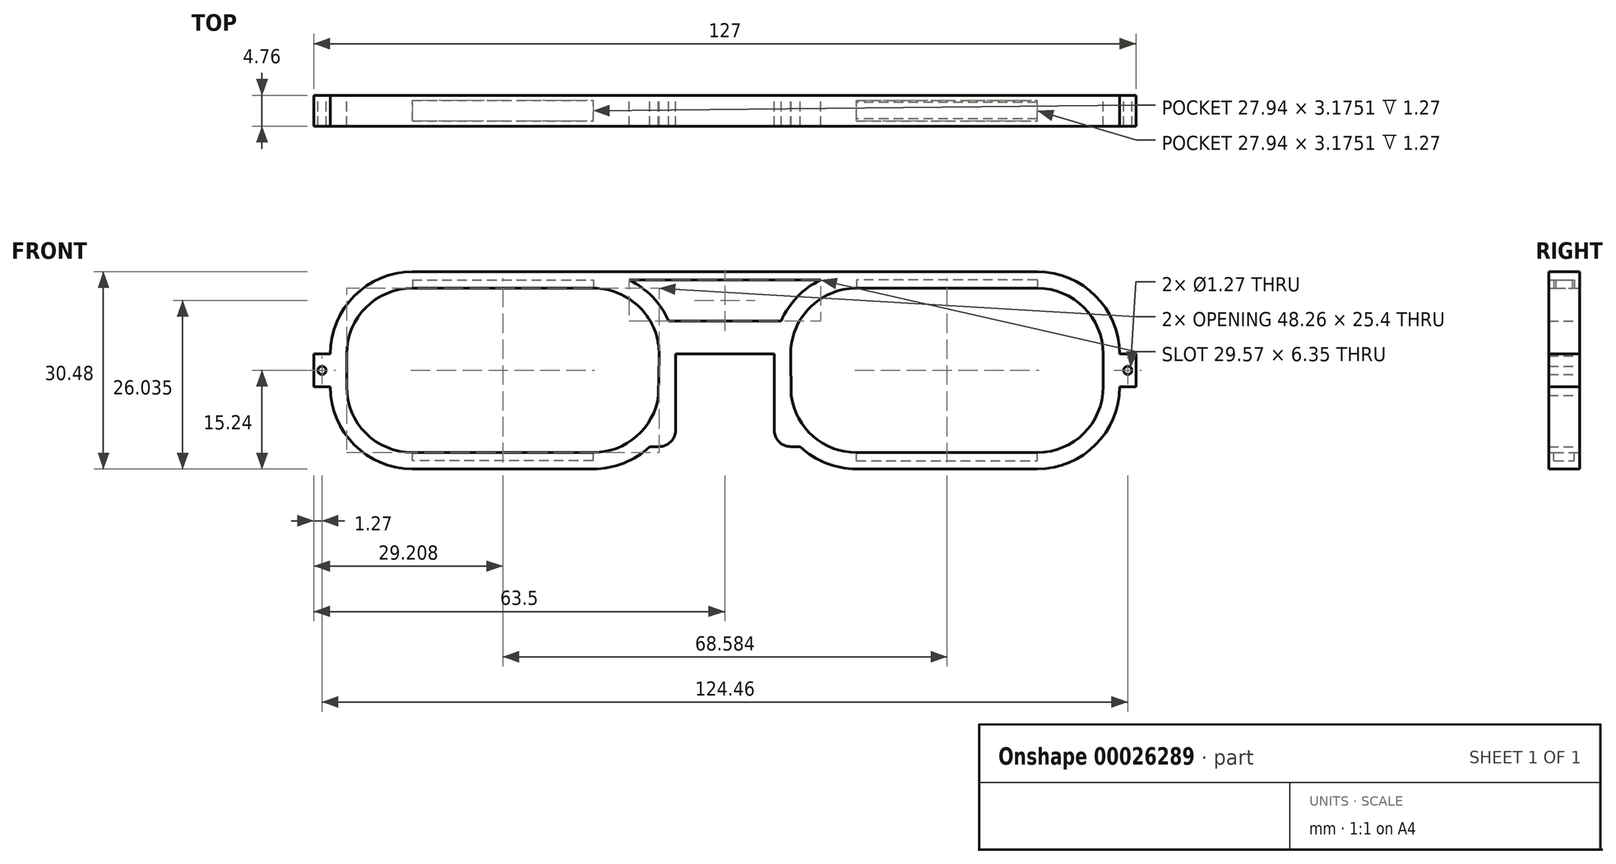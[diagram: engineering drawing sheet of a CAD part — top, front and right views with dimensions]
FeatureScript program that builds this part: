
annotation { "Feature Type Name" : "Feature", "Feature Type Description" : "" }
export const myFeature = defineFeature(function(context is Context, id is Id, definition is map)
    precondition{}
    {
        {
            var Q0;
            Q0=qCreatedBy(makeId("Front.planeOp"),FACE);
            var sketch = newSketch(context, id + "F0", { "sketchPlane" : qUnion([Q0])});
            skLineSegment(sketch, "E0.bottom", {"start": v(12.7, 0) * mm, "end": v(40.64, 0) * mm});
            skLineSegment(sketch, "E0.top", {"start": v(12.7, 30.48) * mm, "end": v(40.64, 30.48) * mm});
            skLineSegment(sketch, "E0.left", {"start": v(0, 12.7) * mm, "end": v(0, 17.78) * mm});
            skLineSegment(sketch, "E0.right", {"start": v(53.34, 12.7) * mm, "end": v(53.34, 17.78) * mm});
            skPoint(sketch, "E1.visualSharp", {"position": v(0, 30.48) * mm});
            skArc(sketch, "E1.filletArc", {"start": v(12.7, 30.48) * mm, "mid": v(3.72, 26.76) * mm, "end": v(0, 17.78) * mm});
            skPoint(sketch, "E2.visualSharp", {"position": v(0, 0) * mm});
            skArc(sketch, "E2.filletArc", {"start": v(0, 12.7) * mm, "mid": v(3.72, 3.72) * mm, "end": v(12.7, 0) * mm});
            skPoint(sketch, "E3.visualSharp", {"position": v(53.34, 0) * mm});
            skArc(sketch, "E3.filletArc", {"start": v(40.64, 0) * mm, "mid": v(45.33, 0.9) * mm, "end": v(49.36, 3.46) * mm});
            skArc(sketch, "E4.filletArc", {"start": v(52.28, 22.86) * mm, "mid": v(49.8, 26.58) * mm, "end": v(46.18, 29.21) * mm});
            skLineSegment(sketch, "E5", {"start": v(40.64, 30.48) * mm, "end": v(68.58, 30.48) * mm});
            skLineSegment(sketch, "E6.MirrorCS", {"start": v(81.28, 30.48) * mm, "end": v(53.34, 30.48) * mm});
            skArc(sketch, "E7.MirrorCS", {"start": v(69.64, 22.86) * mm, "mid": v(72.12, 26.58) * mm, "end": v(75.74, 29.21) * mm});
            skLineSegment(sketch, "E8.MirrorCS", {"start": v(68.58, 12.7) * mm, "end": v(68.58, 17.78) * mm});
            skArc(sketch, "E9.MirrorCS", {"start": v(81.28, 0) * mm, "mid": v(76.6, 0.9) * mm, "end": v(72.56, 3.46) * mm});
            skLineSegment(sketch, "E10.MirrorCS", {"start": v(109.22, 0) * mm, "end": v(81.28, 0) * mm});
            skArc(sketch, "E11.MirrorCS", {"start": v(121.92, 12.7) * mm, "mid": v(118.2, 3.72) * mm, "end": v(109.22, 0) * mm});
            skLineSegment(sketch, "E12.MirrorCS", {"start": v(121.92, 12.7) * mm, "end": v(121.92, 17.78) * mm});
            skArc(sketch, "E13.MirrorCS", {"start": v(109.22, 30.48) * mm, "mid": v(118.2, 26.76) * mm, "end": v(121.92, 17.78) * mm});
            skLineSegment(sketch, "E14.MirrorCS", {"start": v(109.22, 30.48) * mm, "end": v(81.28, 30.48) * mm});
            skLineSegment(sketch, "E15", {"start": v(46.18, 29.21) * mm, "end": v(75.74, 29.21) * mm});
            skLineSegment(sketch, "E16", {"start": v(53.34, 17.78) * mm, "end": v(68.58, 17.78) * mm});
            skLineSegment(sketch, "E17", {"start": v(52.28, 22.86) * mm, "end": v(69.64, 22.86) * mm});
            skPoint(sketch, "E18.end.orphan", {"position": v(53.34, 22.86) * mm});
            skLineSegment(sketch, "E19", {"start": v(53.34, 12.7) * mm, "end": v(53.34, 6) * mm});
            skLineSegment(sketch, "E20", {"start": v(50.8, 3.46) * mm, "end": v(49.36, 3.46) * mm});
            skPoint(sketch, "E21.visualSharp", {"position": v(53.34, 3.46) * mm});
            skArc(sketch, "E21.filletArc", {"start": v(50.8, 3.46) * mm, "mid": v(52.6, 4.2) * mm, "end": v(53.34, 6) * mm});
            skLineSegment(sketch, "E22", {"start": v(68.58, 12.7) * mm, "end": v(68.58, 6) * mm});
            skLineSegment(sketch, "E23", {"start": v(71.12, 3.46) * mm, "end": v(72.56, 3.46) * mm});
            skPoint(sketch, "E24.visualSharp", {"position": v(68.58, 3.46) * mm});
            skArc(sketch, "E24.filletArc", {"start": v(68.58, 6) * mm, "mid": v(69.32, 4.2) * mm, "end": v(71.12, 3.46) * mm});
            skArc(sketch, "E25", {"start": v(81.28, 27.94) * mm, "mid": v(74, 24.86) * mm, "end": v(71.12, 17.5) * mm});
            skArc(sketch, "E26", {"start": v(119.38, 17.78) * mm, "mid": v(116.4, 24.96) * mm, "end": v(109.22, 27.94) * mm});
            skArc(sketch, "E27", {"start": v(71.2, 11.36) * mm, "mid": v(74.59, 5.06) * mm, "end": v(81.28, 2.54) * mm});
            skArc(sketch, "E28", {"start": v(109.22, 2.54) * mm, "mid": v(116.4, 5.52) * mm, "end": v(119.38, 12.7) * mm});
            skLineSegment(sketch, "E29", {"start": v(71.12, 17.78) * mm, "end": v(71.2, 11.36) * mm});
            skLineSegment(sketch, "E30", {"start": v(81.28, 27.94) * mm, "end": v(109.22, 27.94) * mm});
            skLineSegment(sketch, "E31", {"start": v(119.38, 17.78) * mm, "end": v(119.38, 12.7) * mm});
            skLineSegment(sketch, "E32", {"start": v(109.22, 2.54) * mm, "end": v(81.28, 2.54) * mm});
            skArc(sketch, "E33.MirrorCS", {"start": v(40.64, 27.94) * mm, "mid": v(47.92, 24.86) * mm, "end": v(50.8, 17.5) * mm});
            skLineSegment(sketch, "E34.MirrorCS", {"start": v(50.8, 17.78) * mm, "end": v(50.71, 11.36) * mm});
            skArc(sketch, "E35.MirrorCS", {"start": v(50.71, 11.36) * mm, "mid": v(47.33, 5.06) * mm, "end": v(40.64, 2.54) * mm});
            skLineSegment(sketch, "E36.MirrorCS", {"start": v(12.7, 2.54) * mm, "end": v(40.64, 2.54) * mm});
            skArc(sketch, "E37.MirrorCS", {"start": v(12.7, 2.54) * mm, "mid": v(5.52, 5.52) * mm, "end": v(2.54, 12.7) * mm});
            skArc(sketch, "E38.MirrorCS", {"start": v(2.54, 17.78) * mm, "mid": v(5.52, 24.96) * mm, "end": v(12.7, 27.94) * mm});
            skLineSegment(sketch, "E39.MirrorCS", {"start": v(40.64, 27.94) * mm, "end": v(12.7, 27.94) * mm});
            skLineSegment(sketch, "E40.bottom", {"start": v(121.92, 17.78) * mm, "end": v(124.46, 17.78) * mm});
            skLineSegment(sketch, "E40.top", {"start": v(121.92, 12.7) * mm, "end": v(124.46, 12.7) * mm});
            skLineSegment(sketch, "E40.left", {"start": v(121.92, 17.78) * mm, "end": v(121.92, 12.7) * mm});
            skLineSegment(sketch, "E40.right", {"start": v(124.46, 17.78) * mm, "end": v(124.46, 12.7) * mm});
            skLineSegment(sketch, "E41", {"start": v(2.54, 17.78) * mm, "end": v(2.54, 12.7) * mm});
            skLineSegment(sketch, "E42.bottom", {"start": v(0, 17.78) * mm, "end": v(-2.54, 17.78) * mm});
            skLineSegment(sketch, "E42.top", {"start": v(0, 12.7) * mm, "end": v(-2.54, 12.7) * mm});
            skLineSegment(sketch, "E42.left", {"start": v(0, 17.78) * mm, "end": v(0, 12.7) * mm});
            skLineSegment(sketch, "E42.right", {"start": v(-2.54, 17.78) * mm, "end": v(-2.54, 12.7) * mm});
            skLineSegment(sketch, "E43", {"start": v(121.92, 15.24) * mm, "end": v(124.46, 15.24) * mm});
            skLineSegment(sketch, "E44", {"start": v(0, 15.24) * mm, "end": v(-2.54, 15.24) * mm});
            skCircle(sketch, "E45", {"center": v(-1.27, 15.24) * mm, "radius": 0.64 * mm});
            skCircle(sketch, "E46", {"center": v(123.19, 15.24) * mm, "radius": 0.64 * mm});
            skSolve(sketch);
        }
        {
            var Q0;
            Q0=makeQuery(id+"F0.imprint","IMPRINT",FACE,{"disambiguationData":[TD([[makeQuery(id+"F0.imprint","IMPRINT",EDGE,{"derivedFrom":sQuery(id+"F0.wireOp",EDGE,"E0.bottom")}),1.0]])]});
            var Q1;
            {var subQ8=sQuery(id+"F0.wireOp",EDGE,"E42.bottom");Q1=makeQuery(id+"F0.imprint","IMPRINT",FACE,{"disambiguationData":[TD([[makeQuery(id+"F0.imprint","IMPRINT",EDGE,{"derivedFrom":subQ8}),1.0]])]});}
            var Q2;
            {var subQ8=sQuery(id+"F0.wireOp",EDGE,"E42.top");Q2=makeQuery(id+"F0.imprint","IMPRINT",FACE,{"disambiguationData":[TD([[makeQuery(id+"F0.imprint","IMPRINT",EDGE,{"derivedFrom":subQ8}),-1.0]])]});}
            var Q3;
            {var subQ8=sQuery(id+"F0.wireOp",EDGE,"E40.bottom");Q3=makeQuery(id+"F0.imprint","IMPRINT",FACE,{"disambiguationData":[TD([[makeQuery(id+"F0.imprint","IMPRINT",EDGE,{"derivedFrom":subQ8}),-1.0]])]});}
            var Q4;
            {var subQ8=sQuery(id+"F0.wireOp",EDGE,"E40.top");Q4=makeQuery(id+"F0.imprint","IMPRINT",FACE,{"disambiguationData":[TD([[makeQuery(id+"F0.imprint","IMPRINT",EDGE,{"derivedFrom":subQ8}),1.0]])]});}
            extrude(context, id + "F1", {"entities" : qUnion([Q0, Q1, Q2, Q3, Q4]), "depth" : 4.76 * mm});
        }
        {
            var Q0;
            Q0=makeQuery(id+"F1.opExtrude","SWEPT_FACE",FACE,{"disambiguationData":[OSD([sQuery(id+"F0.wireOp",EDGE,"E36.MirrorCS")])]});
            var sketch = newSketch(context, id + "F2", { "sketchPlane" : qUnion([Q0])});
            skLineSegment(sketch, "E47.1", {"start": v(40.64, -4.76) * mm, "end": v(40.64, 0) * mm});
            skLineSegment(sketch, "E47.2", {"start": v(12.7, 0) * mm, "end": v(40.64, 0) * mm});
            skLineSegment(sketch, "E47.3", {"start": v(12.7, -4.76) * mm, "end": v(40.64, -4.76) * mm});
            skLineSegment(sketch, "E47.4", {"start": v(12.7, -4.76) * mm, "end": v(12.7, 0) * mm});
            skLineSegment(sketch, "E48", {"start": v(12.7, -2.38) * mm, "end": v(40.64, -2.38) * mm});
            skLineSegment(sketch, "E49", {"start": v(40.64, -2.38) * mm, "end": v(40.64, -0.8) * mm});
            skLineSegment(sketch, "E50", {"start": v(40.64, -0.8) * mm, "end": v(12.7, -0.8) * mm});
            skLineSegment(sketch, "E51.MirrorCS", {"start": v(40.64, -3.97) * mm, "end": v(12.7, -3.97) * mm});
            skSolve(sketch);
        }
        {
            var Q0;
            {var subQ1=sQuery(id+"F2.wireOp",EDGE,"E48");Q0=makeQuery(id+"F2.imprint","IMPRINT",FACE,{"disambiguationData":[TD([[makeQuery(id+"F2.imprint","IMPRINT",EDGE,{"derivedFrom":subQ1}),1.0]])]});}
            var Q1;
            {var subQ1=sQuery(id+"F2.wireOp",EDGE,"E48");Q1=makeQuery(id+"F2.imprint","IMPRINT",FACE,{"disambiguationData":[TD([[makeQuery(id+"F2.imprint","IMPRINT",EDGE,{"derivedFrom":subQ1}),-1.0]])]});}
            extrude(context, id + "F3", {"entities" : qUnion([Q0, Q1]), "operationType" : NewBodyOperationType.REMOVE, "oppositeDirection" : true, "depth" : 1.27 * mm});
        }
        {
            var Q0;
            Q0=makeQuery(id+"F1.opExtrude","SWEPT_FACE",FACE,{"disambiguationData":[OSD([sQuery(id+"F0.wireOp",EDGE,"E39.MirrorCS")])]});
            var sketch = newSketch(context, id + "F4", { "sketchPlane" : qUnion([Q0])});
            skLineSegment(sketch, "E52", {"start": v(40.64, 2.38) * mm, "end": v(12.7, 2.38) * mm});
            skLineSegment(sketch, "E53", {"start": v(12.7, 2.38) * mm, "end": v(12.7, 0.8) * mm});
            skLineSegment(sketch, "E54", {"start": v(12.7, 0.8) * mm, "end": v(40.64, 0.8) * mm});
            skLineSegment(sketch, "E55.MirrorCS", {"start": v(12.7, 3.97) * mm, "end": v(40.64, 3.97) * mm});
            skSolve(sketch);
        }
        {
            var Q0;
            {var subQ2=sQuery(id+"F4.wireOp",EDGE,"E52");Q0=makeQuery(id+"F4.imprint","IMPRINT",FACE,{"disambiguationData":[TD([[makeQuery(id+"F4.imprint","IMPRINT",EDGE,{"derivedFrom":subQ2}),1.0]])]});}
            var Q1;
            {var subQ3=sQuery(id+"F4.wireOp",EDGE,"E52");Q1=makeQuery(id+"F4.imprint","IMPRINT",FACE,{"disambiguationData":[TD([[makeQuery(id+"F4.imprint","IMPRINT",EDGE,{"derivedFrom":subQ3}),-1.0]])]});}
            extrude(context, id + "F5", {"entities" : qUnion([Q0, Q1]), "operationType" : NewBodyOperationType.REMOVE, "oppositeDirection" : true, "depth" : 1.27 * mm});
        }
        {
            var Q0;
            Q0=makeQuery(id+"F1.opExtrude","SWEPT_FACE",FACE,{"disambiguationData":[OSD([sQuery(id+"F0.wireOp",EDGE,"E30")])]});
            var sketch = newSketch(context, id + "F6", { "sketchPlane" : qUnion([Q0])});
            skLineSegment(sketch, "E56", {"start": v(81.28, 2.38) * mm, "end": v(109.22, 2.38) * mm});
            skLineSegment(sketch, "E57", {"start": v(109.22, 2.38) * mm, "end": v(109.22, 3.65) * mm});
            skLineSegment(sketch, "E58", {"start": v(109.22, 3.65) * mm, "end": v(81.28, 3.65) * mm});
            skLineSegment(sketch, "E59.MirrorCS", {"start": v(109.22, 1.11) * mm, "end": v(81.28, 1.11) * mm});
            skSolve(sketch);
        }
        {
            var Q0;
            {var subQ2=sQuery(id+"F6.wireOp",EDGE,"E56");Q0=makeQuery(id+"F6.imprint","IMPRINT",FACE,{"disambiguationData":[TD([[makeQuery(id+"F6.imprint","IMPRINT",EDGE,{"derivedFrom":subQ2}),1.0]])]});}
            var Q1;
            {var subQ3=sQuery(id+"F6.wireOp",EDGE,"E56");Q1=makeQuery(id+"F6.imprint","IMPRINT",FACE,{"disambiguationData":[TD([[makeQuery(id+"F6.imprint","IMPRINT",EDGE,{"derivedFrom":subQ3}),-1.0]])]});}
            extrude(context, id + "F7", {"entities" : qUnion([Q0, Q1]), "operationType" : NewBodyOperationType.REMOVE, "oppositeDirection" : true, "depth" : 1.27 * mm});
        }
        {
            var Q0;
            Q0=makeQuery(id+"F1.opExtrude","SWEPT_FACE",FACE,{"disambiguationData":[OSD([sQuery(id+"F0.wireOp",EDGE,"E32")])]});
            var sketch = newSketch(context, id + "F8", { "sketchPlane" : qUnion([Q0])});
            skLineSegment(sketch, "E60", {"start": v(109.22, -2.38) * mm, "end": v(81.28, -2.38) * mm});
            skLineSegment(sketch, "E61", {"start": v(81.28, -2.38) * mm, "end": v(81.28, -0.8) * mm});
            skLineSegment(sketch, "E62", {"start": v(81.28, -0.8) * mm, "end": v(109.22, -0.8) * mm});
            skLineSegment(sketch, "E63.MirrorCS", {"start": v(81.28, -3.97) * mm, "end": v(109.22, -3.97) * mm});
            skSolve(sketch);
        }
        {
            var Q0;
            {var subQ3=sQuery(id+"F8.wireOp",EDGE,"E60");Q0=makeQuery(id+"F8.imprint","IMPRINT",FACE,{"disambiguationData":[TD([[makeQuery(id+"F8.imprint","IMPRINT",EDGE,{"derivedFrom":subQ3}),1.0]])]});}
            var Q1;
            {var subQ2=sQuery(id+"F8.wireOp",EDGE,"E60");Q1=makeQuery(id+"F8.imprint","IMPRINT",FACE,{"disambiguationData":[TD([[makeQuery(id+"F8.imprint","IMPRINT",EDGE,{"derivedFrom":subQ2}),-1.0]])]});}
            extrude(context, id + "F9", {"entities" : qUnion([Q0, Q1]), "operationType" : NewBodyOperationType.REMOVE, "oppositeDirection" : true, "depth" : 1.27 * mm});
        }
    });
